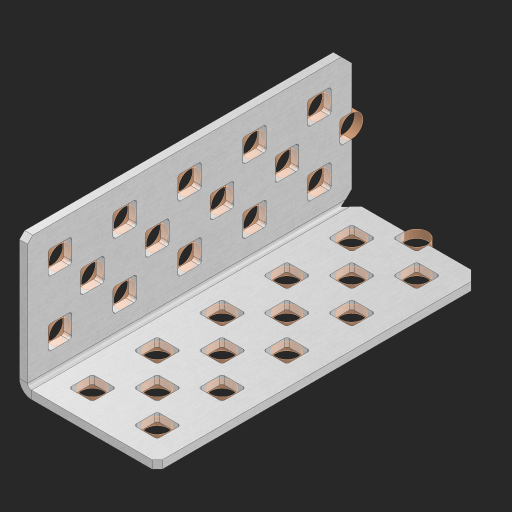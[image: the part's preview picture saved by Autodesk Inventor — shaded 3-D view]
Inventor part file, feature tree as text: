
AUTODESK INVENTOR PART (.ipt)
format: ipt  version: 2023 (Build 270158000, 158)  size: 752,128 bytes
history: native  units: in
note: dims shown in document units (in); Inventor stores cm internally (conversion verified against a paired STEP export)
features: other x36, extrude x28, sheet_metal_op x8, sketch x7, pattern_linear x2, mirror x1, chamfer x1
ambient origin geometry x8: Origin, YZ Plane, XZ Plane, XY Plane, X Axis, Y Axis, Z Axis, Center Point
bodies: Solid1 (feature_tree), Body (feature_tree)
feature tree (83):
  sheet_metal_op  "Flanges"
  sheet_metal_op  "Body Pattern"
  pattern_linear  "Center Pattern"  Spacing1=1.0in  [1 undecoded]
  other  "Arc Length"
  pattern_linear  "Notch Pattern"  Spacing1=0.25in  [1 undecoded]
  other  "Diagonal Plane"
  mirror  "Everything Mirrored"
  chamfer  "End Chamfer"
  sketch  "Sketch1"  dims[d0=1.0in]
  other  "Plate1"
  sketch  "Sketch2"  dims[d1=2.5in]
  other  "Plate2"
  sheet_metal_op  "Bend1"
  sheet_metal_op  "Corner1"
  sketch  "Sketch8"  dims[d2=0.0625in]
  sketch  "Sketch9"  dims[d3=0.0625in]
  other  "Srf91"
  sheet_metal_op  "Body Pattern Sketch"
  other  "Srf92"
  sketch  "Sketch13"  dims[d4=0.0312in]
  sketch  "Sketch15"  dims[d5=0.125in]
  sketch  "Sketch16"  dims[d6=0.0625in d7=1.0in d8=90.0deg d9=0.0312in d10=0.25in d11=0.0625in d12=0.0625in d49=0.182in d50=0.02in d52=0.25in d53=0.0625in d54=0.0in d55=0.172in d56=1.0in d57=0.0in d60=1.9685in d62=0.5in d63=0.7874in d65=0.5in d85=0.1473in d86=0.1782in d89=0.0625in d90=0.0in d91=0.04in d92=0.0491in d95=2.5in d96=0.04in d97=0.25in d98=45.0deg d99=0.25in d106=0.182in d107=0.02in d108=0.5in d110=0.0625in d111=0.0in d112=0.172in d113=0.5in d114=0.0in d117=0.5in d123=0.25in d125=0.25in d126=0.0491in d127=0.1473in d128=0.08in d129=0.04in d130=2.5in]
  other  "Srf786"
  other  "Srf856"
  other  "Srf857"
  other  "Srf858"
  other  "Srf859"
  other  "Srf860"
  other  "Srf861"
  other  "Srf889"
  other  "Srf890"
  other  "Srf891"
  other  "Srf1275"
  other  "Srf1276"
  other  "Srf1278"
  other  "Srf1279"
  other  "Srf1280"
  other  "Srf1281"
  other  "Srf1282"
  other  "Srf1283"
  other  "Srf1277"
  other  "Srf1285"
  other  "Srf1286"
  other  "Srf1287"
  other  "Srf1383"
  other  "Srf1384"
  other  "Srf1445"
  other  "Srf1475"
  other  "Srf1476"
  other  "Srf1537"
  sheet_metal_op  "Body Stamp"
  sheet_metal_op  "Body Circle"
  other  "Center Stamp"
  other  "Center Circle"
  sheet_metal_op  "Notch"
  extrude  "ExtrusionSrf92"  Depth=0.0625in
  extrude  "ExtrusionSrf856"  Depth=0.0625in
  extrude  "ExtrusionSrf857"  Depth=2.5in
  extrude  "ExtrusionSrf858"  Depth=0.02in
  extrude  "ExtrusionSrf859"  Depth=2.5in
  extrude  "ExtrusionSrf860"  Depth=0.0625in
  extrude  "ExtrusionSrf861"  TaperAngle=0.0deg  [1 undecoded]
  extrude  "ExtrusionSrf889"  Depth=2.5in
  extrude  "ExtrusionSrf890"  Depth=1.0in TaperAngle=0.0deg
  extrude  "ExtrusionSrf891"  Depth=2.5in
  extrude  "ExtrusionSrf1275"  Depth=0.5in
  extrude  "ExtrusionSrf1276"  Depth=2.5in
  extrude  "ExtrusionSrf1277"  Depth=2.5in
  extrude  "ExtrusionSrf1278"  Depth=0.0625in
  extrude  "ExtrusionSrf1279"  Depth=2.5in TaperAngle=0.0deg
  extrude  "ExtrusionSrf1280"  Depth=2.5in
  extrude  "ExtrusionSrf1281"  Depth=2.5in TaperAngle=45.0deg
  extrude  "ExtrusionSrf1282"  Depth=2.5in
  extrude  "ExtrusionSrf1345"  Depth=2.5in
  extrude  "ExtrusionSrf1346"  Depth=0.02in
  extrude  "ExtrusionSrf1347"  Depth=0.5in
  extrude  "ExtrusionSrf1348"  Depth=0.0625in
  extrude  "ExtrusionSrf1383"  TaperAngle=0.0deg  [1 undecoded]
  extrude  "ExtrusionSrf1384"  Depth=2.5in
  extrude  "ExtrusionSrf1445"  Depth=0.5in TaperAngle=0.0deg
  extrude  "ExtrusionSrf1475"  Depth=0.5in
  extrude  "ExtrusionSrf1476"  Depth=2.5in
  extrude  "ExtrusionSrf1537"  Depth=2.5in
note: 4 required parameter values undecoded (feature->parameter linkage not recoverable at this tier; creation-order binding heuristic only, values carry confidence <= 0.55)
